# Revit family: PRD_AR_WtrSpplFttngsFrWshBsnsAndTrghs_SelfClosingPillarMixer_F5SM1001,1002,1006,1007
name_source: partatom
category: Plumbing Fixtures
revit_build: Autodesk Revit 2018 (Build: 20190510_1515(x64)
units: mm (PartAtom-declared; Revit-internal decimal feet)

## family parameters
Always vertical = Yes
Cut with Voids When Loaded = No
OmniClass Number = 23.45.55.14
OmniClass Title = Single Faucets
Part Type = Normal
Room Calculation Point = No
Round Connector Dimension = Use Diameter
Shared = No
Work Plane-Based = Yes

## types (4) — shared parameters
AdjustableFlowTime = yes
AssetType = Fixed
Category = Pr_40_20_87_98, Washbasin taps
Color = Chrome
Default Elevation = 1219.2 mm  [stored 4 ft]
Depressurised = no
DiameterNominal = 15 mm
DurationUnit = year
FaucetFunction = MIXED
FaucetMaterial = PRD_AR_ChromatedBrass_HighPolished
FaucetOperation = SELFCLOSING
FaucetType = PILLAR
Finish = high-polished chromium-plated brass
FlowColdWater = 0.1 L/s
FlowHotWater = 0.1 L/s
Form = Self-closing
HygieneFlushing = no
IfcExportAs = IfcValveType
IfcExportType = FAUCET
InletSize = DN 15 (3/8 inch.)
Manufacturer = KWC Group AG
ManufacturerName = KWC Group AG
ManufacturerURL = www.kwc.com
Material = Brass
MaterialsBody = Brass
MaterialsFinishAndColour = high-polished chromium-plated brass
MaximumFlowTime = 35.00 seconds
MinimumFlowPressure = 0.50 bar
MinimumFlowTime = 5.00 seconds
NBSDescription = Water supply fittings for wash basins and troughs
NBSReference = 45-35-70/371
OutletMaterial = PRD_AR_SyntheticGrey
ProductInformation = https://pim.kwc.com
ProtectiveShutdown = no
SoundInsulation = no
SpoutProjection = 125.00 mm
ThermalDisinfection = no
TypeOfMixing = yes
TypeOfMounting = Taphole
TypeOfOperation = Manual Operation
TypeOfTap = pillar tap
URL = www.kwc.com
Uniclass2015Code = Pr_40_20_87_98
Uniclass2015Title = Washbasin taps
Uniclass2015Version = Products v1.7
Version = 1
WarrantyDurationUnit = year
zero-valued in all types: NominalHeight, NominalLength, NominalWidth

## per-type parameters (varying)
| type | BIMObjectName | Description | FlowRateMaximum | GrossWeight | Model | ModelNumber | ModelReference | Name | NetWeight |
| F5SM1001 - 0.08 L/s connection via hoses | PRD_AR_WaterSupplyFittingsForWashBasinsAndTroughs_SelfClosingPillarMixer_F5SM1001 | F5S-Mix self-closing pillar mixer DN 15 as single-mixer tap for sanitary facilities. FRAMIC self-closing mixing cartridge, hydraulically controlled, low-maintenance and stagnation-free, with ceramic disc technology, self-closing, flow pressure-independent due to medium-separated design. Stepless adjustment of flow duration. With adjustable, turn-proof temperature stop. For connection to hot water and cold water via hoses with integrated backflow preventer and strainers. All-metal construction, high-polished chromium-plated brass. Anti-theft aerator, SLIM design, with integrated flow regulator 5.0 l/min. | 0.08 L/s at 3 bar | 1.76 kg | F5SM1001 | 2030036163 | F5SM1001 | F5 self-closing pillar mixer F5SM1001 | 1.66 kg |
| F5SM1006 - 0.05 L/s connection via hoses | PRD_AR_WaterSupplyFittingsForWashBasinsAndTroughs_SelfClosingPillarMixer_F5SM1006 | F5S-Mix self-closing pillar mixer DN 15 as single-mixer tap for sanitary facilities. FRAMIC self-closing mixing cartridge, hydraulically controlled, low-maintenance and stagnation-free, with ceramic disc technology, self-closing, flow pressure-independent due to medium-separated design. Stepless adjustment of flow duration. With adjustable, turn-proof temperature stop. For connection to hot water and cold water via hoses with integrated backflow preventer and strainers. All-metal construction, high-polished chromium-plated brass. Aerator with integrated flow regulator 3.0 l/min. | 0.05 L/s at 3 bar | 1.76 kg | F5SM1006 | 2030039396 | F5SM1006 | F5 self-closing pillar mixer F5SM1006 | 1.7 kg |
| F5SM1002 - 0.08 L/s connection via pipes | PRD_AR_WaterSupplyFittingsForWashBasinsAndTroughs_SelfClosingPillarMixer_F5SM1002 | F5S-Mix self-closing pillar mixer DN 15 as single-mixer tap for sanitary facilities. FRAMIC self-closing mixing cartridge, hydraulically controlled, low-maintenance and stagnation-free, with ceramic disc technology, self-closing, flow pressure-independent due to medium-separated design. Stepless adjustment of flow duration. With adjustable, turn-proof temperature stop. For connection to hot water and cold water via pipes with integrated backflow preventer and strainers. All-metal construction, high-polished chromium-plated brass. Anti-theft aerator, SLIM design, with integrated flow regulator 5.0 l/min. | 0.08 L/s at 3 bar | 1.98 kg | F5SM1002 | 2030036164 | F5SM1002 | F5 self-closing pillar mixer F5SM1002 | 1.85 kg |
| F5SM1007 - 0.05 L/s connection via pipes | PRD_AR_WaterSupplyFittingsForWashBasinsAndTroughs_SelfClosingPillarMixer_F5SM1007 | F5S-Mix self-closing pillar mixer DN 15 as single-mixer tap for sanitary facilities. FRAMIC self-closing mixing cartridge, hydraulically controlled, low-maintenance and stagnation-free, with ceramic disc technology, self-closing, flow pressure-independent due to medium-separated design. Stepless adjustment of flow duration. With adjustable, turn-proof temperature stop. For connection to hot water and cold water via pipes with integrated backflow preventer and strainers. All-metal construction, high-polished chromium-plated brass. Aerator with integrated flow regulator 3.0 l/min. | 0.05 L/s at 3 bar | 2.1 kg | F5SM1007 | 2030039404 | F5SM1007 | F5 self-closing pillar mixer F5SM1007 | 1.9 kg |

note: [stored X ft] marks values corroborated as IEEE doubles in the binary element streams (Revit-internal decimal feet)

## geometry (parser evidence)
native form markers: Sweep x2
no freeform markers — native parametric forms only
